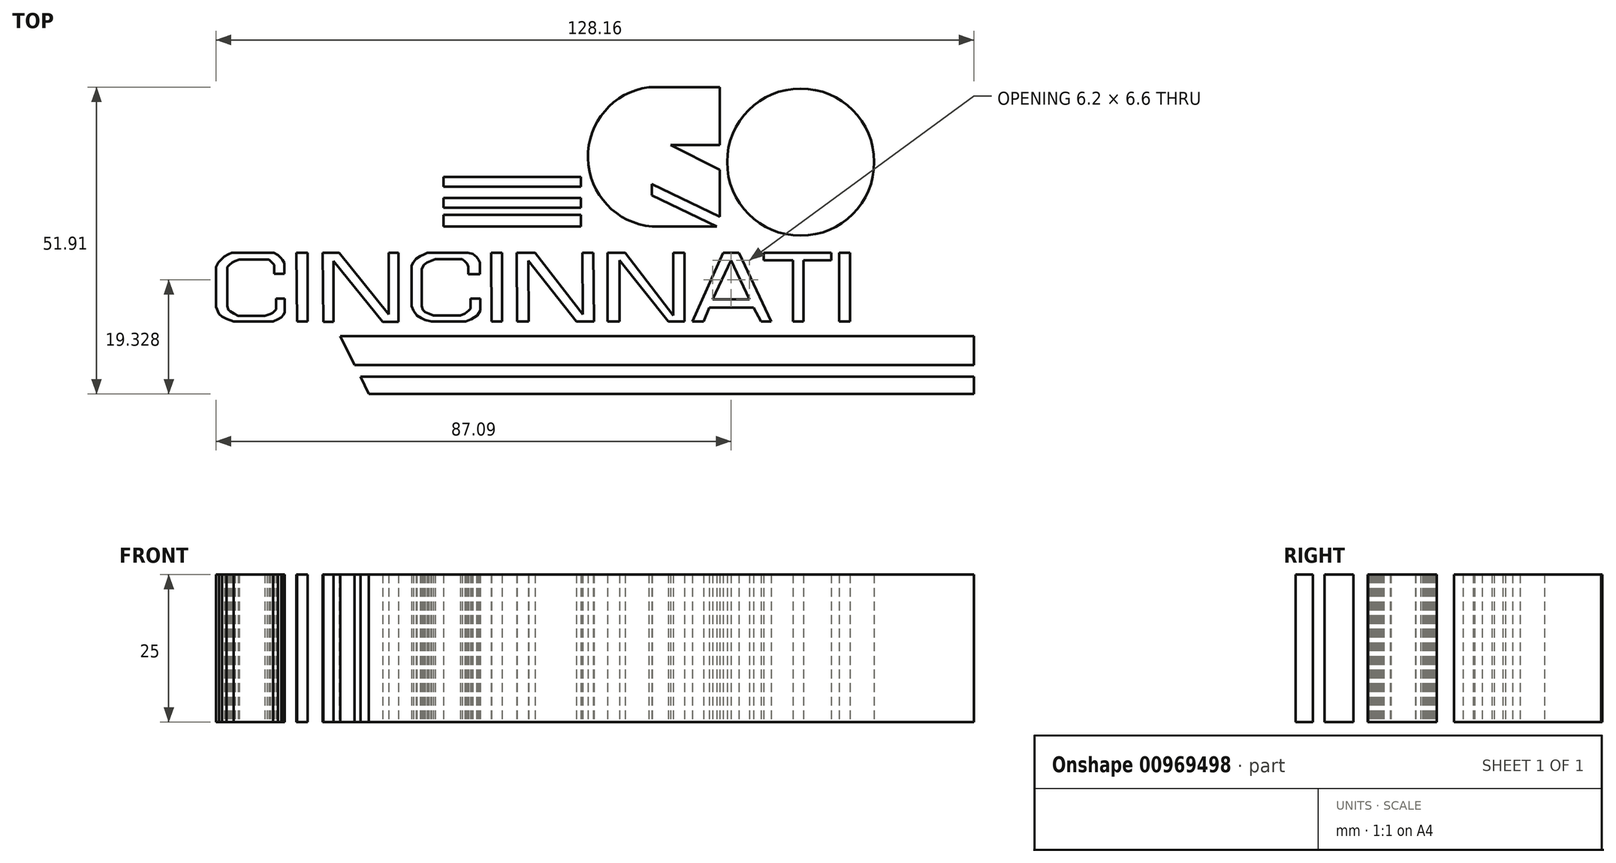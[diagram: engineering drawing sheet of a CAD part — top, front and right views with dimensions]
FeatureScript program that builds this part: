
annotation { "Feature Type Name" : "Feature", "Feature Type Description" : "" }
export const myFeature = defineFeature(function(context is Context, id is Id, definition is map)
    precondition{}
    {
        {
            var Q0;
            Q0=qCreatedBy(makeId("Top.planeOp"),FACE);
            var sketch = newSketch(context, id + "F0", { "sketchPlane" : qUnion([Q0])});
            skLineSegment(sketch, "E0", {"start": v(0, 51.91) * mm, "end": v(1.04, 49.91) * mm});
            skLineSegment(sketch, "E1", {"start": v(1.04, 49.91) * mm, "end": v(13.85, 49.91) * mm});
            skLineSegment(sketch, "E2", {"start": v(1.87, 48.3) * mm, "end": v(13.02, 48.3) * mm});
            skLineSegment(sketch, "E3", {"start": v(2.66, 46.78) * mm, "end": v(12.23, 46.78) * mm});
            skLineSegment(sketch, "E4", {"start": v(11.33, 45.05) * mm, "end": v(3.56, 45.05) * mm});
            skLineSegment(sketch, "E5", {"start": v(3.56, 45.05) * mm, "end": v(4.4, 43.44) * mm});
            skLineSegment(sketch, "E6", {"start": v(4.4, 43.44) * mm, "end": v(10.49, 43.44) * mm});
            skLineSegment(sketch, "E7", {"start": v(9.92, 42.34) * mm, "end": v(4.97, 42.34) * mm});
            skLineSegment(sketch, "E8", {"start": v(4.97, 42.34) * mm, "end": v(12.03, 28.56) * mm});
            skLineSegment(sketch, "E9", {"start": v(12.03, 28.56) * mm, "end": v(23.5, 51.91) * mm});
            skLineSegment(sketch, "E10", {"start": v(26.45, 51.91) * mm, "end": v(14.83, 28.56) * mm});
            skLineSegment(sketch, "E11", {"start": v(14.83, 28.56) * mm, "end": v(38, 28.56) * mm});
            skLineSegment(sketch, "E12", {"start": v(38, 28.56) * mm, "end": v(26.45, 51.91) * mm});
            skLineSegment(sketch, "E13", {"start": v(19.65, 38.23) * mm, "end": v(21.66, 38.23) * mm});
            skLineSegment(sketch, "E14", {"start": v(21.66, 38.23) * mm, "end": v(22.65, 36.22) * mm});
            skLineSegment(sketch, "E15", {"start": v(22.65, 36.22) * mm, "end": v(18.65, 36.22) * mm});
            skLineSegment(sketch, "E16", {"start": v(21.66, 38.23) * mm, "end": v(26.41, 28.56) * mm, "construction": true});
            skLineSegment(sketch, "E17", {"start": v(17.83, 34.57) * mm, "end": v(23.46, 34.57) * mm});
            skLineSegment(sketch, "E18", {"start": v(23.46, 34.57) * mm, "end": v(24.22, 33.02) * mm});
            skLineSegment(sketch, "E19", {"start": v(24.22, 33.02) * mm, "end": v(17.05, 33.02) * mm});
            skLineSegment(sketch, "E20", {"start": v(24.05, 33.36) * mm, "end": v(25, 31.45) * mm});
            skLineSegment(sketch, "E21", {"start": v(25, 31.45) * mm, "end": v(16.27, 31.45) * mm});
            skLineSegment(sketch, "E22", {"start": v(25.34, 30.74) * mm, "end": v(25.64, 30.12) * mm});
            skLineSegment(sketch, "E23", {"start": v(25.64, 30.12) * mm, "end": v(15.61, 30.12) * mm});
            skLineSegment(sketch, "E24", {"start": v(39.28, 51.91) * mm, "end": v(51.32, 51.91) * mm});
            skLineSegment(sketch, "E25", {"start": v(51.32, 51.91) * mm, "end": v(51.32, 39.4) * mm});
            skLineSegment(sketch, "E26", {"start": v(51.32, 39.4) * mm, "end": v(62.52, 39.4) * mm});
            skLineSegment(sketch, "E27", {"start": v(62.52, 37.98) * mm, "end": v(39.28, 37.98) * mm});
            skLineSegment(sketch, "E28", {"start": v(39.28, 37.98) * mm, "end": v(39.28, 51.91) * mm});
            skLineSegment(sketch, "E29", {"start": v(39.28, 28.32) * mm, "end": v(62.52, 28.32) * mm, "construction": true});
            skLineSegment(sketch, "E30", {"start": v(39.28, 36.71) * mm, "end": v(62.52, 36.71) * mm});
            skLineSegment(sketch, "E31", {"start": v(39.28, 35.09) * mm, "end": v(62.52, 35.09) * mm});
            skLineSegment(sketch, "E32", {"start": v(39.28, 33.19) * mm, "end": v(62.52, 33.19) * mm});
            skLineSegment(sketch, "E33", {"start": v(62.52, 31.54) * mm, "end": v(39.28, 31.54) * mm});
            skLineSegment(sketch, "E34", {"start": v(39.28, 30.28) * mm, "end": v(62.52, 30.28) * mm});
            skLineSegment(sketch, "E35", {"start": v(39.28, 28.32) * mm, "end": v(62.52, 28.32) * mm});
            skLineSegment(sketch, "E36", {"start": v(86, 42.11) * mm, "end": v(86, 51.91) * mm});
            skLineSegment(sketch, "E37", {"start": v(86, 51.91) * mm, "end": v(74, 51.91) * mm});
            skLineSegment(sketch, "E38", {"start": v(86, 42.11) * mm, "end": v(77.68, 42.11) * mm});
            skLineSegment(sketch, "E39", {"start": v(77.68, 42.11) * mm, "end": v(86, 37.95) * mm});
            skLineSegment(sketch, "E40", {"start": v(86, 37.95) * mm, "end": v(86, 28.33) * mm, "construction": true});
            skLineSegment(sketch, "E41", {"start": v(86, 28.33) * mm, "end": v(74.56, 28.33) * mm, "construction": true});
            skLineSegment(sketch, "E42", {"start": v(74.28, 39.91) * mm, "end": v(86, 34.05) * mm});
            skLineSegment(sketch, "E43", {"start": v(86, 34.05) * mm, "end": v(86, 37.95) * mm});
            skLineSegment(sketch, "E44", {"start": v(86, 35.46) * mm, "end": v(86, 30.01) * mm});
            skLineSegment(sketch, "E45", {"start": v(86, 30.01) * mm, "end": v(74.52, 35.53) * mm});
            skLineSegment(sketch, "E46", {"start": v(86, 33.27) * mm, "end": v(86, 29.15) * mm});
            skLineSegment(sketch, "E47", {"start": v(86, 30.04) * mm, "end": v(86, 29.38) * mm});
            skLineSegment(sketch, "E48", {"start": v(74.52, 33.62) * mm, "end": v(85.52, 28.33) * mm});
            skLineSegment(sketch, "E49", {"start": v(74.56, 28.33) * mm, "end": v(86, 28.33) * mm});
            skArc(sketch, "E50", {"start": v(74, 51.91) * mm, "mid": v(63.7, 39.87) * mm, "end": v(74.56, 28.33) * mm});
            skLineSegment(sketch, "E51", {"start": v(98.4, 47.7) * mm, "end": v(98.4, 28.06) * mm, "construction": true});
            skLineSegment(sketch, "E52", {"start": v(98.4, 47.7) * mm, "end": v(93.35, 49.94) * mm});
            skLineSegment(sketch, "E53", {"start": v(98.4, 46.57) * mm, "end": v(92.47, 49.36) * mm});
            skLineSegment(sketch, "E54", {"start": v(98.4, 45.27) * mm, "end": v(91.49, 48.59) * mm});
            skLineSegment(sketch, "E55", {"start": v(98.4, 44.11) * mm, "end": v(90.7, 47.83) * mm});
            skLineSegment(sketch, "E56", {"start": v(90.02, 47.06) * mm, "end": v(98.4, 42.9) * mm});
            skLineSegment(sketch, "E57", {"start": v(89.43, 46.26) * mm, "end": v(98.4, 41.86) * mm});
            skLineSegment(sketch, "E58", {"start": v(88.76, 45.18) * mm, "end": v(98.4, 40.32) * mm});
            skLineSegment(sketch, "E59", {"start": v(88.35, 44.34) * mm, "end": v(98.4, 39.28) * mm});
            skCircle(sketch, "E60", {"center": v(99.69, 39.23) * mm, "radius": 12.44 * mm});
            skPoint(sketch, "E60.second.point", {"position": v(112.13, 39.34) * mm});
            skPoint(sketch, "E60.third.point", {"position": v(105.73, 28.36) * mm});
            skLineSegment(sketch, "E61", {"start": v(21.83, 9.8) * mm, "end": v(128.97, 9.8) * mm});
            skLineSegment(sketch, "E62", {"start": v(21.83, 9.8) * mm, "end": v(26.64, 0) * mm, "construction": true});
            skLineSegment(sketch, "E63", {"start": v(21.83, 9.8) * mm, "end": v(24.23, 4.9) * mm});
            skLineSegment(sketch, "E64", {"start": v(24.23, 4.9) * mm, "end": v(128.97, 4.9) * mm});
            skLineSegment(sketch, "E65", {"start": v(25.2, 2.91) * mm, "end": v(128.97, 2.91) * mm});
            skLineSegment(sketch, "E66", {"start": v(25.2, 2.91) * mm, "end": v(26.64, 0) * mm});
            skLineSegment(sketch, "E67", {"start": v(26.64, 0) * mm, "end": v(128.97, 0) * mm});
            skLineSegment(sketch, "E68", {"start": v(128.97, 2.91) * mm, "end": v(128.97, 0) * mm});
            skLineSegment(sketch, "E69", {"start": v(128.97, 9.8) * mm, "end": v(128.97, 4.9) * mm});
            skLineSegment(sketch, "E70", {"start": v(10.93, 20.34) * mm, "end": v(12.32, 20.34) * mm});
            skLineSegment(sketch, "E71", {"start": v(12.32, 20.34) * mm, "end": v(12.32, 22.16) * mm});
            skLineSegment(sketch, "E72", {"start": v(12.32, 22.16) * mm, "end": v(12.05, 22.69) * mm});
            skLineSegment(sketch, "E73", {"start": v(12.05, 22.69) * mm, "end": v(11.8, 23) * mm});
            skLineSegment(sketch, "E74", {"start": v(11.8, 23) * mm, "end": v(11.28, 23.5) * mm});
            skLineSegment(sketch, "E75", {"start": v(11.28, 23.5) * mm, "end": v(10.55, 23.88) * mm});
            skLineSegment(sketch, "E76", {"start": v(10.55, 23.88) * mm, "end": v(3.47, 23.88) * mm});
            skLineSegment(sketch, "E77", {"start": v(3.47, 23.88) * mm, "end": v(2.9, 23.67) * mm});
            skLineSegment(sketch, "E78", {"start": v(2.9, 23.67) * mm, "end": v(2.16, 23.25) * mm});
            skLineSegment(sketch, "E79", {"start": v(2.16, 23.25) * mm, "end": v(1.7, 22.77) * mm});
            skLineSegment(sketch, "E80", {"start": v(1.7, 22.77) * mm, "end": v(1.17, 22.22) * mm});
            skLineSegment(sketch, "E81", {"start": v(1.17, 22.22) * mm, "end": v(0.81, 21.5) * mm});
            skLineSegment(sketch, "E82", {"start": v(0.81, 21.5) * mm, "end": v(0.81, 14.74) * mm});
            skLineSegment(sketch, "E83", {"start": v(0.81, 14.74) * mm, "end": v(1.28, 13.56) * mm});
            skLineSegment(sketch, "E84", {"start": v(1.28, 13.56) * mm, "end": v(1.8, 13.07) * mm});
            skLineSegment(sketch, "E85", {"start": v(1.8, 13.07) * mm, "end": v(2.54, 12.7) * mm});
            skLineSegment(sketch, "E86", {"start": v(2.54, 12.7) * mm, "end": v(3.77, 12.25) * mm});
            skLineSegment(sketch, "E87", {"start": v(3.77, 12.25) * mm, "end": v(10.47, 12.25) * mm});
            skLineSegment(sketch, "E88", {"start": v(10.47, 12.25) * mm, "end": v(11.28, 12.64) * mm});
            skLineSegment(sketch, "E89", {"start": v(11.28, 12.64) * mm, "end": v(11.82, 12.97) * mm});
            skLineSegment(sketch, "E90", {"start": v(11.82, 12.97) * mm, "end": v(12.17, 13.33) * mm});
            skLineSegment(sketch, "E91", {"start": v(12.17, 13.33) * mm, "end": v(12.4, 13.8) * mm});
            skLineSegment(sketch, "E92", {"start": v(12.4, 13.8) * mm, "end": v(12.4, 14.18) * mm});
            skLineSegment(sketch, "E93", {"start": v(12.4, 14.18) * mm, "end": v(12.4, 16.12) * mm});
            skLineSegment(sketch, "E94", {"start": v(12.4, 16.12) * mm, "end": v(10.94, 16.12) * mm});
            skLineSegment(sketch, "E95", {"start": v(10.94, 16.12) * mm, "end": v(10.94, 14.33) * mm});
            skLineSegment(sketch, "E96", {"start": v(10.94, 14.33) * mm, "end": v(10.7, 14.07) * mm});
            skLineSegment(sketch, "E97", {"start": v(10.7, 14.07) * mm, "end": v(10.39, 13.75) * mm});
            skLineSegment(sketch, "E98", {"start": v(10.39, 13.75) * mm, "end": v(10.03, 13.52) * mm});
            skLineSegment(sketch, "E99", {"start": v(10.03, 13.52) * mm, "end": v(9.44, 13.35) * mm});
            skLineSegment(sketch, "E100", {"start": v(9.44, 13.35) * mm, "end": v(9.03, 13.25) * mm});
            skLineSegment(sketch, "E101", {"start": v(9.03, 13.25) * mm, "end": v(4.54, 13.25) * mm});
            skLineSegment(sketch, "E102", {"start": v(4.54, 13.25) * mm, "end": v(3.83, 13.61) * mm});
            skLineSegment(sketch, "E103", {"start": v(3.83, 13.61) * mm, "end": v(3.2, 13.99) * mm});
            skLineSegment(sketch, "E104", {"start": v(3.2, 13.99) * mm, "end": v(2.91, 14.27) * mm});
            skLineSegment(sketch, "E105", {"start": v(2.91, 14.27) * mm, "end": v(2.7, 14.9) * mm});
            skLineSegment(sketch, "E106", {"start": v(2.7, 14.9) * mm, "end": v(2.7, 15.78) * mm});
            skLineSegment(sketch, "E107", {"start": v(2.7, 15.78) * mm, "end": v(2.7, 20.84) * mm});
            skLineSegment(sketch, "E108", {"start": v(2.7, 20.84) * mm, "end": v(2.7, 21.5) * mm});
            skLineSegment(sketch, "E109", {"start": v(2.7, 21.5) * mm, "end": v(3, 21.8) * mm});
            skLineSegment(sketch, "E110", {"start": v(3, 21.8) * mm, "end": v(3.54, 22.23) * mm});
            skLineSegment(sketch, "E111", {"start": v(3.54, 22.23) * mm, "end": v(4.06, 22.5) * mm});
            skLineSegment(sketch, "E112", {"start": v(4.06, 22.5) * mm, "end": v(4.73, 22.73) * mm});
            skLineSegment(sketch, "E113", {"start": v(4.73, 22.73) * mm, "end": v(9.75, 22.73) * mm});
            skLineSegment(sketch, "E114", {"start": v(9.75, 22.73) * mm, "end": v(10.22, 22.27) * mm});
            skLineSegment(sketch, "E115", {"start": v(10.22, 22.27) * mm, "end": v(10.64, 21.86) * mm});
            skLineSegment(sketch, "E116", {"start": v(10.64, 21.86) * mm, "end": v(10.64, 20.34) * mm});
            skLineSegment(sketch, "E117", {"start": v(10.64, 20.34) * mm, "end": v(10.93, 20.34) * mm});
            skLineSegment(sketch, "E118", {"start": v(14.4, 23.88) * mm, "end": v(16.26, 23.88) * mm});
            skLineSegment(sketch, "E119", {"start": v(16.26, 23.88) * mm, "end": v(16.26, 12.28) * mm});
            skLineSegment(sketch, "E120", {"start": v(16.26, 12.28) * mm, "end": v(14.48, 12.28) * mm});
            skLineSegment(sketch, "E121", {"start": v(14.48, 12.28) * mm, "end": v(14.4, 23.88) * mm});
            skLineSegment(sketch, "E122", {"start": v(18.92, 12.21) * mm, "end": v(20.64, 12.21) * mm});
            skLineSegment(sketch, "E123", {"start": v(20.64, 12.21) * mm, "end": v(20.64, 22.51) * mm});
            skLineSegment(sketch, "E124", {"start": v(20.64, 22.51) * mm, "end": v(29, 12.21) * mm});
            skLineSegment(sketch, "E125", {"start": v(29, 12.21) * mm, "end": v(31.67, 12.21) * mm});
            skLineSegment(sketch, "E126", {"start": v(31.67, 12.21) * mm, "end": v(31.67, 23.88) * mm});
            skLineSegment(sketch, "E127", {"start": v(31.67, 23.88) * mm, "end": v(30, 23.88) * mm});
            skLineSegment(sketch, "E128", {"start": v(30, 23.88) * mm, "end": v(30, 13.5) * mm});
            skLineSegment(sketch, "E129", {"start": v(30, 13.5) * mm, "end": v(21.62, 23.88) * mm});
            skLineSegment(sketch, "E130", {"start": v(21.62, 23.88) * mm, "end": v(18.85, 23.88) * mm});
            skLineSegment(sketch, "E131", {"start": v(18.85, 23.88) * mm, "end": v(18.92, 12.21) * mm});
            skLineSegment(sketch, "E132.bottom", {"start": v(0.81, 12.25) * mm, "end": v(108.05, 12.25) * mm, "construction": true});
            skLineSegment(sketch, "E132.top", {"start": v(0.81, 23.88) * mm, "end": v(108.05, 23.88) * mm, "construction": true});
            skLineSegment(sketch, "E132.left", {"start": v(0.81, 12.25) * mm, "end": v(0.81, 23.88) * mm, "construction": true});
            skLineSegment(sketch, "E132.right", {"start": v(108.05, 12.25) * mm, "end": v(108.05, 23.88) * mm});
            skLineSegment(sketch, "E133", {"start": v(43.47, 20.28) * mm, "end": v(45.4, 20.28) * mm});
            skLineSegment(sketch, "E134", {"start": v(45.4, 20.28) * mm, "end": v(45.4, 22.24) * mm});
            skLineSegment(sketch, "E135", {"start": v(45.4, 22.24) * mm, "end": v(45.21, 22.73) * mm});
            skLineSegment(sketch, "E136", {"start": v(45.21, 22.73) * mm, "end": v(44.86, 23.18) * mm});
            skLineSegment(sketch, "E137", {"start": v(44.86, 23.18) * mm, "end": v(44.22, 23.67) * mm});
            skLineSegment(sketch, "E138", {"start": v(44.22, 23.67) * mm, "end": v(43.38, 23.88) * mm});
            skLineSegment(sketch, "E139", {"start": v(43.38, 23.88) * mm, "end": v(36.52, 23.88) * mm});
            skLineSegment(sketch, "E140", {"start": v(36.52, 23.88) * mm, "end": v(36.02, 23.65) * mm});
            skLineSegment(sketch, "E141", {"start": v(36.02, 23.65) * mm, "end": v(35.35, 23.33) * mm});
            skLineSegment(sketch, "E142", {"start": v(35.35, 23.33) * mm, "end": v(34.61, 22.86) * mm});
            skLineSegment(sketch, "E143", {"start": v(34.61, 22.86) * mm, "end": v(34.17, 22.31) * mm});
            skLineSegment(sketch, "E144", {"start": v(34.17, 22.31) * mm, "end": v(33.84, 21.72) * mm});
            skLineSegment(sketch, "E145", {"start": v(33.84, 21.72) * mm, "end": v(33.84, 14.88) * mm});
            skLineSegment(sketch, "E146", {"start": v(33.84, 14.88) * mm, "end": v(34.2, 14.09) * mm});
            skLineSegment(sketch, "E147", {"start": v(34.2, 14.09) * mm, "end": v(34.73, 13.3) * mm});
            skLineSegment(sketch, "E148", {"start": v(34.73, 13.3) * mm, "end": v(35.55, 12.83) * mm});
            skLineSegment(sketch, "E149", {"start": v(35.55, 12.83) * mm, "end": v(36.17, 12.5) * mm});
            skLineSegment(sketch, "E150", {"start": v(36.17, 12.5) * mm, "end": v(37.21, 12.25) * mm});
            skLineSegment(sketch, "E151", {"start": v(37.21, 12.25) * mm, "end": v(43.03, 12.25) * mm});
            skLineSegment(sketch, "E152", {"start": v(43.03, 12.25) * mm, "end": v(43.97, 12.68) * mm});
            skLineSegment(sketch, "E153", {"start": v(43.97, 12.68) * mm, "end": v(45.01, 13.27) * mm});
            skLineSegment(sketch, "E154", {"start": v(45.01, 13.27) * mm, "end": v(45.5, 14.11) * mm});
            skLineSegment(sketch, "E155", {"start": v(45.5, 14.11) * mm, "end": v(45.5, 16.17) * mm});
            skLineSegment(sketch, "E156", {"start": v(45.5, 16.17) * mm, "end": v(43.82, 16.17) * mm});
            skLineSegment(sketch, "E157", {"start": v(43.82, 16.17) * mm, "end": v(43.82, 14.46) * mm});
            skLineSegment(sketch, "E158", {"start": v(43.82, 14.46) * mm, "end": v(43.55, 14.09) * mm});
            skLineSegment(sketch, "E159", {"start": v(43.55, 14.09) * mm, "end": v(42.9, 13.6) * mm});
            skLineSegment(sketch, "E160", {"start": v(42.9, 13.6) * mm, "end": v(42.9, 13.6) * mm});
            skLineSegment(sketch, "E161", {"start": v(42.9, 13.6) * mm, "end": v(42.11, 13.3) * mm});
            skLineSegment(sketch, "E162", {"start": v(42.11, 13.3) * mm, "end": v(37.58, 13.3) * mm});
            skLineSegment(sketch, "E163", {"start": v(37.58, 13.3) * mm, "end": v(36.76, 13.6) * mm});
            skLineSegment(sketch, "E164", {"start": v(36.76, 13.6) * mm, "end": v(36.14, 13.89) * mm});
            skLineSegment(sketch, "E165", {"start": v(36.14, 13.89) * mm, "end": v(35.8, 14.22) * mm});
            skLineSegment(sketch, "E166", {"start": v(35.8, 14.22) * mm, "end": v(35.62, 14.84) * mm});
            skLineSegment(sketch, "E167", {"start": v(35.62, 14.84) * mm, "end": v(35.62, 21.18) * mm});
            skLineSegment(sketch, "E168", {"start": v(35.62, 21.18) * mm, "end": v(35.95, 21.88) * mm});
            skLineSegment(sketch, "E169", {"start": v(35.95, 21.88) * mm, "end": v(36.5, 22.22) * mm});
            skLineSegment(sketch, "E170", {"start": v(36.5, 22.22) * mm, "end": v(37.1, 22.5) * mm});
            skLineSegment(sketch, "E171", {"start": v(37.1, 22.5) * mm, "end": v(37.89, 22.8) * mm});
            skLineSegment(sketch, "E172", {"start": v(37.89, 22.8) * mm, "end": v(42.43, 22.8) * mm});
            skLineSegment(sketch, "E173", {"start": v(42.43, 22.8) * mm, "end": v(42.9, 22.45) * mm});
            skLineSegment(sketch, "E174", {"start": v(42.9, 22.45) * mm, "end": v(43.3, 22.03) * mm});
            skLineSegment(sketch, "E175", {"start": v(43.3, 22.03) * mm, "end": v(43.47, 21.55) * mm});
            skLineSegment(sketch, "E176", {"start": v(43.47, 21.55) * mm, "end": v(43.47, 20.28) * mm});
            skLineSegment(sketch, "E177", {"start": v(47.32, 23.88) * mm, "end": v(49.2, 23.88) * mm});
            skLineSegment(sketch, "E178", {"start": v(49.2, 23.88) * mm, "end": v(49.2, 12.25) * mm});
            skLineSegment(sketch, "E179", {"start": v(49.2, 12.25) * mm, "end": v(47.4, 12.25) * mm});
            skLineSegment(sketch, "E180", {"start": v(47.4, 12.25) * mm, "end": v(47.32, 23.88) * mm});
            skLineSegment(sketch, "E181", {"start": v(51.7, 12.25) * mm, "end": v(53.69, 12.25) * mm});
            skLineSegment(sketch, "E182", {"start": v(53.69, 12.25) * mm, "end": v(53.61, 22.56) * mm});
            skLineSegment(sketch, "E183", {"start": v(53.61, 22.56) * mm, "end": v(61.77, 12.25) * mm});
            skLineSegment(sketch, "E184", {"start": v(61.77, 12.25) * mm, "end": v(64.7, 12.25) * mm});
            skLineSegment(sketch, "E185", {"start": v(64.7, 12.25) * mm, "end": v(64.63, 23.88) * mm});
            skLineSegment(sketch, "E186", {"start": v(64.63, 23.88) * mm, "end": v(62.78, 23.88) * mm});
            skLineSegment(sketch, "E187", {"start": v(62.78, 23.88) * mm, "end": v(62.86, 13.5) * mm});
            skLineSegment(sketch, "E188", {"start": v(62.86, 13.5) * mm, "end": v(54.8, 23.88) * mm});
            skLineSegment(sketch, "E189", {"start": v(54.8, 23.88) * mm, "end": v(51.68, 23.88) * mm});
            skLineSegment(sketch, "E190", {"start": v(51.68, 23.88) * mm, "end": v(51.7, 12.25) * mm});
            skLineSegment(sketch, "E191", {"start": v(67.03, 23.88) * mm, "end": v(67.03, 12.25) * mm});
            skLineSegment(sketch, "E192", {"start": v(67.03, 12.25) * mm, "end": v(69.03, 12.25) * mm});
            skLineSegment(sketch, "E193", {"start": v(69.03, 12.25) * mm, "end": v(69.03, 22.63) * mm});
            skLineSegment(sketch, "E194", {"start": v(69.03, 22.63) * mm, "end": v(77.28, 12.25) * mm});
            skLineSegment(sketch, "E195", {"start": v(77.28, 12.25) * mm, "end": v(80.07, 12.25) * mm});
            skLineSegment(sketch, "E196", {"start": v(80.07, 12.25) * mm, "end": v(80.07, 23.88) * mm});
            skLineSegment(sketch, "E197", {"start": v(80.07, 23.88) * mm, "end": v(78.14, 23.88) * mm});
            skLineSegment(sketch, "E198", {"start": v(78.14, 23.88) * mm, "end": v(78.14, 13.32) * mm});
            skLineSegment(sketch, "E199", {"start": v(78.14, 13.32) * mm, "end": v(70.02, 23.88) * mm});
            skLineSegment(sketch, "E200", {"start": v(70.02, 23.88) * mm, "end": v(67.03, 23.88) * mm});
            skLineSegment(sketch, "E201", {"start": v(81.35, 12.25) * mm, "end": v(86.57, 23.88) * mm});
            skLineSegment(sketch, "E202", {"start": v(86.57, 23.88) * mm, "end": v(89.26, 23.88) * mm});
            skLineSegment(sketch, "E203", {"start": v(89.26, 23.88) * mm, "end": v(94.7, 12.25) * mm});
            skLineSegment(sketch, "E204", {"start": v(94.7, 12.25) * mm, "end": v(92.97, 12.25) * mm});
            skLineSegment(sketch, "E205", {"start": v(92.97, 12.25) * mm, "end": v(91.75, 14.6) * mm});
            skLineSegment(sketch, "E206", {"start": v(91.75, 14.6) * mm, "end": v(84.25, 14.6) * mm});
            skLineSegment(sketch, "E207", {"start": v(84.25, 14.6) * mm, "end": v(83.3, 12.25) * mm});
            skLineSegment(sketch, "E208", {"start": v(83.3, 12.25) * mm, "end": v(81.35, 12.25) * mm});
            skLineSegment(sketch, "E209", {"start": v(87.92, 22.63) * mm, "end": v(84.8, 16.03) * mm});
            skLineSegment(sketch, "E210", {"start": v(84.8, 16.03) * mm, "end": v(91, 16.03) * mm});
            skLineSegment(sketch, "E211", {"start": v(91, 16.03) * mm, "end": v(87.92, 22.63) * mm});
            skLineSegment(sketch, "E212", {"start": v(93.42, 23.88) * mm, "end": v(104.87, 23.88) * mm});
            skLineSegment(sketch, "E213", {"start": v(104.87, 23.88) * mm, "end": v(104.87, 22.63) * mm});
            skLineSegment(sketch, "E214", {"start": v(104.87, 22.63) * mm, "end": v(100.15, 22.63) * mm});
            skLineSegment(sketch, "E215", {"start": v(100.15, 22.63) * mm, "end": v(100.15, 12.25) * mm});
            skLineSegment(sketch, "E216", {"start": v(100.15, 12.25) * mm, "end": v(98.37, 12.25) * mm});
            skLineSegment(sketch, "E217", {"start": v(98.37, 12.25) * mm, "end": v(98.37, 22.63) * mm});
            skLineSegment(sketch, "E218", {"start": v(98.37, 22.63) * mm, "end": v(93.42, 22.63) * mm});
            skLineSegment(sketch, "E219", {"start": v(93.42, 22.63) * mm, "end": v(93.42, 23.88) * mm});
            skLineSegment(sketch, "E220.bottom", {"start": v(106.2, 23.88) * mm, "end": v(108.05, 23.88) * mm});
            skLineSegment(sketch, "E220.top", {"start": v(106.2, 12.25) * mm, "end": v(108.05, 12.25) * mm});
            skLineSegment(sketch, "E220.left", {"start": v(106.2, 23.88) * mm, "end": v(106.2, 12.25) * mm});
            skLineSegment(sketch, "E220.right", {"start": v(108.05, 23.88) * mm, "end": v(108.05, 12.25) * mm});
            skLineSegment(sketch, "E221", {"start": v(0, 51.91) * mm, "end": v(23.5, 51.91) * mm});
            skLineSegment(sketch, "E222", {"start": v(98.4, 47.7) * mm, "end": v(98.4, 46.57) * mm});
            skLineSegment(sketch, "E223", {"start": v(98.4, 45.27) * mm, "end": v(98.4, 44.11) * mm});
            skLineSegment(sketch, "E224", {"start": v(98.4, 42.9) * mm, "end": v(98.4, 41.86) * mm});
            skLineSegment(sketch, "E225", {"start": v(98.4, 40.32) * mm, "end": v(98.4, 39.28) * mm});
            skLineSegment(sketch, "E226", {"start": v(0, 51.91) * mm, "end": v(4.97, 42.34) * mm, "construction": true});
            skLineSegment(sketch, "E227", {"start": v(1.87, 48.3) * mm, "end": v(2.66, 46.78) * mm});
            skLineSegment(sketch, "E228", {"start": v(13.85, 49.91) * mm, "end": v(14.89, 51.91) * mm});
            skLineSegment(sketch, "E229", {"start": v(13.02, 48.3) * mm, "end": v(12.23, 46.78) * mm});
            skLineSegment(sketch, "E230", {"start": v(11.33, 45.05) * mm, "end": v(10.49, 43.44) * mm});
            skLineSegment(sketch, "E231", {"start": v(39.28, 37.98) * mm, "end": v(39.28, 28.32) * mm, "construction": true});
            skLineSegment(sketch, "E232", {"start": v(62.52, 39.4) * mm, "end": v(62.52, 28.32) * mm, "construction": true});
            skLineSegment(sketch, "E233", {"start": v(39.28, 36.71) * mm, "end": v(39.28, 35.09) * mm});
            skLineSegment(sketch, "E234", {"start": v(39.28, 33.19) * mm, "end": v(39.28, 31.54) * mm});
            skLineSegment(sketch, "E235", {"start": v(39.28, 30.28) * mm, "end": v(39.28, 28.32) * mm});
            skLineSegment(sketch, "E236", {"start": v(62.52, 28.32) * mm, "end": v(62.52, 30.28) * mm});
            skLineSegment(sketch, "E237", {"start": v(62.52, 31.54) * mm, "end": v(62.52, 33.19) * mm});
            skLineSegment(sketch, "E238", {"start": v(62.52, 35.09) * mm, "end": v(62.52, 36.71) * mm});
            skLineSegment(sketch, "E239", {"start": v(74.52, 37.96) * mm, "end": v(86, 32.18) * mm});
            skLineSegment(sketch, "E240", {"start": v(74.52, 33.62) * mm, "end": v(74.52, 35.53) * mm});
            skLineSegment(sketch, "E241", {"start": v(86, 36) * mm, "end": v(74.47, 41.96) * mm});
            skSolve(sketch);
        }
        {
            var Q0;
            Q0=makeQuery(id+"F0.imprint","IMPRINT",FACE,{"disambiguationData":[TD([[makeQuery(id+"F0.imprint","IMPRINT",EDGE,{"derivedFrom":sQuery(id+"F0.wireOp",EDGE,"E30")}),-1.0]])]});
            var Q1;
            Q1=makeQuery(id+"F0.imprint","IMPRINT",FACE,{"disambiguationData":[TD([[makeQuery(id+"F0.imprint","IMPRINT",EDGE,{"derivedFrom":sQuery(id+"F0.wireOp",EDGE,"E32")}),-1.0]])]});
            var Q2;
            Q2=makeQuery(id+"F0.imprint","IMPRINT",FACE,{"disambiguationData":[TD([[makeQuery(id+"F0.imprint","IMPRINT",EDGE,{"derivedFrom":sQuery(id+"F0.wireOp",EDGE,"E34")}),-1.0]])]});
            var Q3;
            Q3=makeQuery(id+"F0.imprint","IMPRINT",FACE,{"disambiguationData":[TD([[makeQuery(id+"F0.imprint","IMPRINT",EDGE,{"derivedFrom":sQuery(id+"F0.wireOp",EDGE,"E36")}),1.0]])]});
            var Q4;
            Q4=makeQuery(id+"F0.imprint","IMPRINT",FACE,{"disambiguationData":[TD([[makeQuery(id+"F0.imprint","IMPRINT",EDGE,{"derivedFrom":sQuery(id+"F0.wireOp",EDGE,"E61")}),-1.0]])]});
            var Q5;
            Q5=makeQuery(id+"F0.imprint","IMPRINT",FACE,{"disambiguationData":[TD([[makeQuery(id+"F0.imprint","IMPRINT",EDGE,{"derivedFrom":sQuery(id+"F0.wireOp",EDGE,"E65")}),-1.0]])]});
            var Q6;
            Q6=makeQuery(id+"F0.imprint","IMPRINT",FACE,{"disambiguationData":[TD([[makeQuery(id+"F0.imprint","IMPRINT",EDGE,{"derivedFrom":sQuery(id+"F0.wireOp",EDGE,"E70")}),1.0]])]});
            var Q7;
            Q7=makeQuery(id+"F0.imprint","IMPRINT",FACE,{"disambiguationData":[TD([[makeQuery(id+"F0.imprint","IMPRINT",EDGE,{"derivedFrom":sQuery(id+"F0.wireOp",EDGE,"E118")}),-1.0]])]});
            var Q8;
            Q8=makeQuery(id+"F0.imprint","IMPRINT",FACE,{"disambiguationData":[TD([[makeQuery(id+"F0.imprint","IMPRINT",EDGE,{"derivedFrom":sQuery(id+"F0.wireOp",EDGE,"E122")}),1.0]])]});
            var Q9;
            Q9=makeQuery(id+"F0.imprint","IMPRINT",FACE,{"disambiguationData":[TD([[makeQuery(id+"F0.imprint","IMPRINT",EDGE,{"derivedFrom":sQuery(id+"F0.wireOp",EDGE,"E133")}),1.0]])]});
            var Q10;
            Q10=makeQuery(id+"F0.imprint","IMPRINT",FACE,{"disambiguationData":[TD([[makeQuery(id+"F0.imprint","IMPRINT",EDGE,{"derivedFrom":sQuery(id+"F0.wireOp",EDGE,"E177")}),-1.0]])]});
            var Q11;
            Q11=makeQuery(id+"F0.imprint","IMPRINT",FACE,{"disambiguationData":[TD([[makeQuery(id+"F0.imprint","IMPRINT",EDGE,{"derivedFrom":sQuery(id+"F0.wireOp",EDGE,"E181")}),1.0]])]});
            var Q12;
            Q12=makeQuery(id+"F0.imprint","IMPRINT",FACE,{"disambiguationData":[TD([[makeQuery(id+"F0.imprint","IMPRINT",EDGE,{"derivedFrom":sQuery(id+"F0.wireOp",EDGE,"E191")}),1.0]])]});
            var Q13;
            Q13=makeQuery(id+"F0.imprint","IMPRINT",FACE,{"disambiguationData":[TD([[makeQuery(id+"F0.imprint","IMPRINT",EDGE,{"derivedFrom":sQuery(id+"F0.wireOp",EDGE,"E212")}),-1.0]])]});
            var Q14;
            Q14=makeQuery(id+"F0.imprint","IMPRINT",FACE,{"disambiguationData":[TD([[makeQuery(id+"F0.imprint","IMPRINT",EDGE,{"derivedFrom":sQuery(id+"F0.wireOp",EDGE,"E220.bottom")}),-1.0]])]});
            var Q15;
            {var subQ0=sQuery(id+"F0.wireOp",EDGE,"E52");Q15=makeQuery(id+"F0.imprint","IMPRINT",FACE,{"disambiguationData":[TD([[makeQuery(id+"F0.imprint","IMPRINT",EDGE,{"derivedFrom":subQ0}),1.0]])]});}
            var Q16;
            {var subQ0=sQuery(id+"F0.wireOp",EDGE,"E54");Q16=makeQuery(id+"F0.imprint","IMPRINT",FACE,{"disambiguationData":[TD([[makeQuery(id+"F0.imprint","IMPRINT",EDGE,{"derivedFrom":subQ0}),1.0]])]});}
            var Q17;
            {var subQ0=sQuery(id+"F0.wireOp",EDGE,"E56");Q17=makeQuery(id+"F0.imprint","IMPRINT",FACE,{"disambiguationData":[TD([[makeQuery(id+"F0.imprint","IMPRINT",EDGE,{"derivedFrom":subQ0}),-1.0]])]});}
            var Q18;
            {var subQ0=sQuery(id+"F0.wireOp",EDGE,"E58");Q18=makeQuery(id+"F0.imprint","IMPRINT",FACE,{"disambiguationData":[TD([[makeQuery(id+"F0.imprint","IMPRINT",EDGE,{"derivedFrom":subQ0}),-1.0]])]});}
            var Q19;
            Q19=makeQuery(id+"F0.imprint","IMPRINT",FACE,{"disambiguationData":[TD([[makeQuery(id+"F0.imprint","IMPRINT",EDGE,{"derivedFrom":sQuery(id+"F0.wireOp",EDGE,"E201")}),-1.0]])]});
            var Q20;
            {var subQ8=sQuery(id+"F0.wireOp",EDGE,"E52");Q20=makeQuery(id+"F0.imprint","IMPRINT",FACE,{"disambiguationData":[TD([[makeQuery(id+"F0.imprint","IMPRINT",EDGE,{"derivedFrom":subQ8}),-1.0]])]});}
            extrude(context, id + "F1", {"entities" : qUnion([Q0, Q1, Q2, Q3, Q4, Q5, Q6, Q7, Q8, Q9, Q10, Q11, Q12, Q13, Q14, Q15, Q16, Q17, Q18, Q19, Q20]), "depth" : 25 * mm, "offsetDistance" : 25 * mm});
        }
    });
